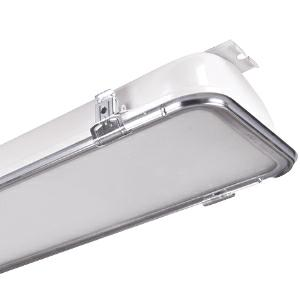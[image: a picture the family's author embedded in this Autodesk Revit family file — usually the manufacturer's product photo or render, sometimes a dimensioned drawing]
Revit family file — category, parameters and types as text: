
# Revit family: 3f_filippi_-_beta_235_76_vs_ampio_3f_filippi_-_52902_-_beta_235_led_762x45_dali_ampio_vs_l1265
name_source: partatom
category: Lighting Fixtures
units: mm (PartAtom-declared; Revit-internal decimal feet)

## family parameters
Cut with Voids When Loaded = No
Host = Face
Light Source = No
Part Type = Normal
Room Calculation Point = No
Round Connector Dimension = Use Diameter
Shared = No

## types (1)
- 3F Filippi - Beta 235 76 VS Ampio (1 x LED, 12803 lm, 92 W, 4000 K)
    Apparent Load = 92 VA
    Approval mark = CE
    CIE Flux Codes = 65 90 98 100 100
    Color Rendering = 80
    Color Temperature = 4000 K
    Control Gear = Electronic transformer
    Default Elevation = 1800 mm
    Description = ILLUMINOTECHNICAL
Luminous efficiency 100% (DLOR 100%, ULOR 0%).
Initial luminous flux of the luminaire 12803 lm.
Wide symmetric distribution.
Installation Interdistance Transv.D = 1.26 x hu - Long.D = 1.32 x hu.
Tabular UGR (CIE 117 - 4H-8H; S=0.25H; 70/50/20): RUG 21.8 - 22.9.
Beam angle: 87° - 92°.
Luminous efficacy 139 lm/W.
Lifetime (L93/B10): 30000 h. (tq+25°C)
Lifetime (L90/B10): 50000 h. (tq+25°C)
Lifetime (L85/B10): 80000 h. (tq+25°C)
Lifetime (L80/B10): 100000 h. (tq+25°C)
Lifetime (L85/B10): 50000 h. (tq+45°C)
Sudden decreased luminous flux after 50000 hours: 0% (C0).
Photobiological safety in compliance with IEC/TR 62778: RG0 risk exempt, (IEC 62471).
In compliance with IEC/EN 62722-2-1 - IEC/EN 62717 standards.

SOURCE
2 linear LED modules 45W/840.
Energy efficiency class (UE 2019/2020 - UE 2019/2015): C.
CIE 13.3 Colour rendering index: CRI >80 (R9 <50%).
IES TM-30 Fidelity Index: Rf = 84 Rg = 95.
CCT nominal colour temperature 4000 K.
Colour initial tolerance (MacAdam): SDCM 3.

MECHANICAL
Single-piece housing in pressed steel, powder-coated in white epoxy-polyester.
VS moulded anti-glare glass, non-combustible, single-piece perimeter frame in galvanised steel.
Ecologic anti-aging injected sealing gasket.
Oversized gear-tray reflector unit in highly reflective white painted hot-galvanised steel.
Methacrylate (PMMA) lenses with external flat surface.
Galvanised steel snap-lock clips for diffuser mounting (safety n° 4 per fixture).
Luminaire with limited surface temperature. - D - (EN 60598-2-24)
Dimensions: 1265x235 mm, height 105 mm. Weight 9.94 kg.
IP66 protection degree.
Mechanical strength to impacts IK09 (10 joule).
Glow-wire test resistance 960°C.

ELECTRICAL
Halogen Free DALI-2 DATI (Parts 251, 252, 253), PUSH-DIM, electronic wiring 230V-50/60Hz, power factor 0.95 at full load, THD <25%, constant output current, class I, 1 driver, 1 DALI addresse.
Power of the luminaire 92 W.
ENEC - CE.
Flicker: <4%.
Luminaire compliant with EN 60598-2-22 for power supply from a centralised emergency system CPSS (Central Power Supply System), not incorporated in the luminaire - high risk areas excluded. The default power and flux are 100% in AC and 15% in DC.
Ambient temperature from -20°C to +45°C.
Temperature class T6 max 85°C.
Quick connection via M25 5P connector with 9-13 mm tightening range.
Relative humidity UR: <85%.

INSTALLATION
Ceiling / Suspended / Wall.
All accessories dedicated to this product are available on the Catalog and on our website www.3F-Filippi.com.

APPLICATIONS
Dry, dusty indoor environments, subject to occasional water splashes.
Industrial environments, warehouses, environments where security locks are required on all clips, e.g. prisons (on request).
Environments in which it is necessary a total protection against falling fragments (eg environments with foodstuffs or machines with moving parts or with extreme temperature changes), use luminaires with laminated glass.
Tempered glass is not immune to falling fragments from harmless and caused by shocks or exceptionally derived from the tempering process.

LIGHT MANAGEMENT
Recommended minimum setting: 10%.
The luminaire, equipped with (DALI-2 DATI) driver, can be controlled manually with 3F Easy Dim technology or automatically/manually with wired or wireless DALI/D2D control systems.
The D2D driver guarantees interoperability with other devices with the same certification by making the following information available:
Device Data (Part 251), Energy Report (Part 252), Diagnosis & Maintenance (Part 253).
In electrical systems without a regulation system (manual or automatic) and DALI bus, a suitable jumper must be made on the DA-DA terminals of the appliance.

WARNING
Fixture not suitable for cold stores with an ambient temperature <0°C and/or relative humidity >85%.
Luminaire designed for disposal/recycling at end-of-life.
Replaceable (LED only) light source by a professional. Replaceable control gear by a professional.
    Height = 105 mm
    Lamp = 1 x LED
    Lamp Light Flux = 12803 lm
    Lamp Power = 92 W
    Lamp count = 1
    Length = 1265 mm
    Lifetime = 50000 h
    Luminous efficacy = 139 lm/W
    Manufacturer = 3F Filippi
    ModVariant = No
    Model = 3F Filippi - 52902 - Beta 235 LED 762x45 DALI AMPIO VS L1265
    Mounting Place = Ceiling
    Mounting Type = Pendant
    Number of Poles = 1
    OnlyDefault = Yes
    Power Factor = 1
    Product Name = 3F Filippi - Beta 235 76 VS Ampio
    Product group = pendant luminaire
    ProductGroupID = 9
    Protection Class = Protection class I
    Protection Degree = IP 66
    RLX_Detail_Level = 1
    RLX_Emergency_Light_Flux = 0 lm
    RLX_Emergency_Type = 0
    RLX_Emergency_Type_DB = No
    RlxData = <blob elided: 83645 chars, md5=ab1c23fe>
    Socket = socket
    Standby Power = 0 W
    System Light Flux = 12803 lm
    System Power = 92 W
    Type Comments = Product without accessories
    Type Image = 3ffilippi_52902.jpg
    URL = http://relux.com
    VarID = ---
    Voltage = 0 V
    Weight = 0.00 kg
    Width = 235 mm

## geometry (parser evidence)
native form markers: Blend x4, Sweep x11
no freeform markers — native parametric forms only
